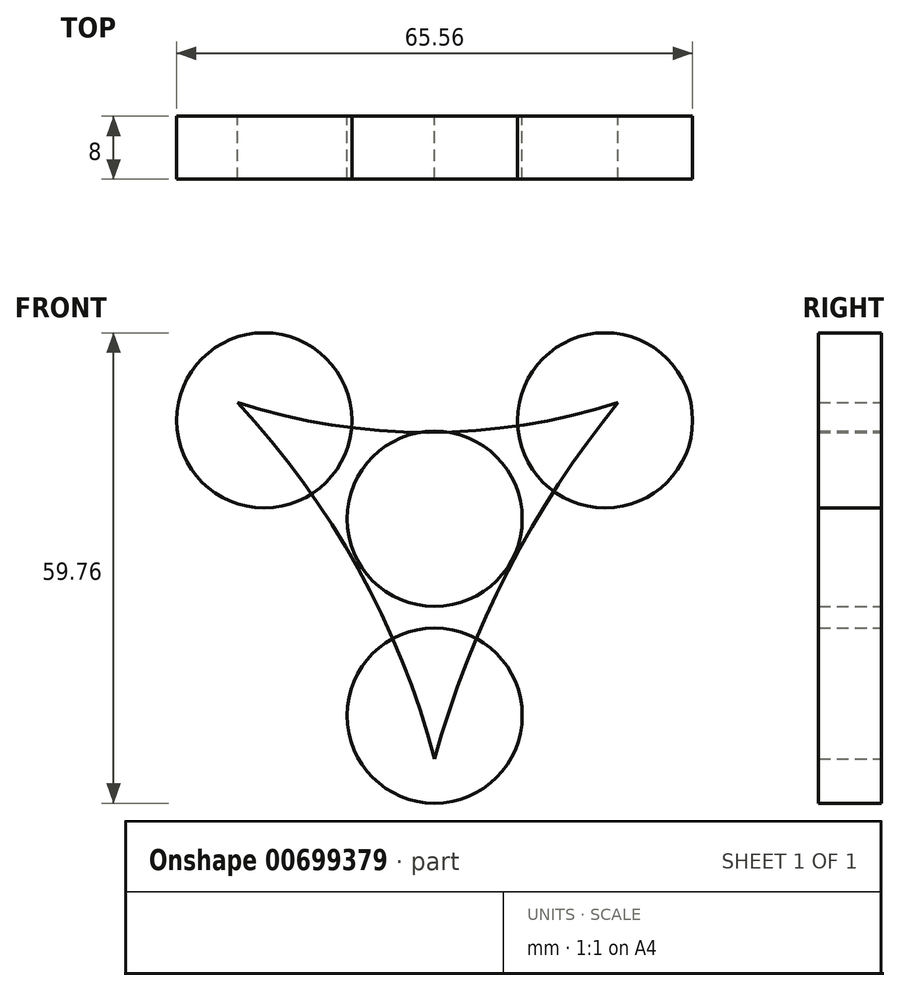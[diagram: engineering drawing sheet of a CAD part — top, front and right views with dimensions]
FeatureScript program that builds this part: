
annotation { "Feature Type Name" : "Feature", "Feature Type Description" : "" }
export const myFeature = defineFeature(function(context is Context, id is Id, definition is map)
    precondition{}
    {
        {
            var Q0;
            Q0=qCreatedBy(makeId("Front.planeOp"),FACE);
            var sketch = newSketch(context, id + "F0", { "sketchPlane" : qUnion([Q0])});
            skCircle(sketch, "E0", {"center": v(0, 0) * mm, "radius": 11.12 * mm});
            skCircle(sketch, "E1", {"center": v(21.65, 12.5) * mm, "radius": 11.12 * mm});
            skCircle(sketch, "E2", {"center": v(-21.65, 12.5) * mm, "radius": 11.12 * mm});
            skCircle(sketch, "E3", {"center": v(0, -25) * mm, "radius": 11.12 * mm});
            skLineSegment(sketch, "E4", {"start": v(0, 0) * mm, "end": v(21.65, 12.5) * mm});
            skLineSegment(sketch, "E5", {"start": v(0, 0) * mm, "end": v(0, -25) * mm});
            skLineSegment(sketch, "E6", {"start": v(0, 0) * mm, "end": v(-21.65, 12.5) * mm});
            skSolve(sketch);
        }
        {
            var Q0;
            Q0=qCreatedBy(makeId("Front.planeOp"),FACE);
            var sketch = newSketch(context, id + "F1", { "sketchPlane" : qUnion([Q0])});
            skArc(sketch, "E7", {"start": v(-1.61, -25) * mm, "mid": v(0.02, -25.06) * mm, "end": v(1.65, -25) * mm});
            skArc(sketch, "E8", {"start": v(0, -30.5) * mm, "mid": v(-9.72, -6.31) * mm, "end": v(-25.05, 14.76) * mm});
            skArc(sketch, "E9", {"start": v(23.3, 14.76) * mm, "mid": v(9.3, -6.66) * mm, "end": v(0, -30.5) * mm});
            skArc(sketch, "E10", {"start": v(-25.05, 14.76) * mm, "mid": v(-0.87, 10.97) * mm, "end": v(23.3, 14.76) * mm});
            skArc(sketch, "E11.trimOffspring", {"start": v(21.63, 12.65) * mm, "mid": v(21.22, 13.33) * mm, "end": v(20.78, 14) * mm});
            skArc(sketch, "E12.trimOffspring", {"start": v(-21.05, 13.59) * mm, "mid": v(-21.65, 12.6) * mm, "end": v(-22.2, 11.6) * mm});
            skSolve(sketch);
        }
        {
            var Q0;
            {var subQ0=sQuery(id+"F1.wireOp",EDGE,"E7");Q0=makeQuery(id+"F1.imprint","IMPRINT",FACE,{"disambiguationData":[TD([[makeQuery(id+"F1.imprint","IMPRINT",EDGE,{"derivedFrom":subQ0}),-1.0]])]});}
            var Q1;
            {var subQ4=sQuery(id+"F1.wireOp",EDGE,"E7");Q1=makeQuery(id+"F1.imprint","IMPRINT",FACE,{"disambiguationData":[TD([[makeQuery(id+"F1.imprint","IMPRINT",EDGE,{"derivedFrom":subQ4}),1.0]])]});}
            var Q2;
            Q2=makeQuery(id+"F0.imprint","IMPRINT",FACE,{"disambiguationData":[TD([[makeQuery(id+"F0.imprint","IMPRINT",EDGE,{"derivedFrom":sQuery(id+"F0.wireOp",EDGE,"E3")}),1.0]])]});
            var Q3;
            {var subQ0=sQuery(id+"F0.wireOp",EDGE,"E6");var subQ1=sQuery(id+"F0.wireOp",EDGE,"E0");var subQ2=makeQuery(id+"F0.imprint","INTERSECT",VERTEX,{"derivedFrom":[subQ1,subQ0]});Q3=makeQuery(id+"F0.imprint","IMPRINT",FACE,{"disambiguationData":[TD([[makeQuery(id+"F0.imprint","IMPRINT",EDGE,{"disambiguationData":[TD([[subQ2,1.0]])],"derivedFrom":subQ1}),1.0]])]});}
            var Q4;
            {var subQ0=sQuery(id+"F0.wireOp",EDGE,"E6");var subQ1=sQuery(id+"F0.wireOp",EDGE,"E0");var subQ2=makeQuery(id+"F0.imprint","INTERSECT",VERTEX,{"derivedFrom":[subQ1,subQ0]});Q4=makeQuery(id+"F0.imprint","IMPRINT",FACE,{"disambiguationData":[TD([[makeQuery(id+"F0.imprint","IMPRINT",EDGE,{"disambiguationData":[TD([[subQ2,-1.0]])],"derivedFrom":subQ1}),1.0]])]});}
            var Q5;
            {var subQ0=sQuery(id+"F0.wireOp",EDGE,"E4");var subQ1=sQuery(id+"F0.wireOp",EDGE,"E0");var subQ2=makeQuery(id+"F0.imprint","INTERSECT",VERTEX,{"derivedFrom":[subQ1,subQ0]});Q5=makeQuery(id+"F0.imprint","IMPRINT",FACE,{"disambiguationData":[TD([[makeQuery(id+"F0.imprint","IMPRINT",EDGE,{"disambiguationData":[TD([[subQ2,1.0]])],"derivedFrom":subQ1}),1.0]])]});}
            var Q6;
            {var subQ3=sQuery(id+"F1.wireOp",EDGE,"E12.trimOffspring");Q6=makeQuery(id+"F1.imprint","IMPRINT",FACE,{"disambiguationData":[TD([[makeQuery(id+"F1.imprint","IMPRINT",EDGE,{"derivedFrom":subQ3}),-1.0]])]});}
            var Q7;
            {var subQ3=sQuery(id+"F1.wireOp",EDGE,"E11.trimOffspring");Q7=makeQuery(id+"F1.imprint","IMPRINT",FACE,{"disambiguationData":[TD([[makeQuery(id+"F1.imprint","IMPRINT",EDGE,{"derivedFrom":subQ3}),-1.0]])]});}
            var Q8;
            Q8=makeQuery(id+"F0.imprint","IMPRINT",FACE,{"disambiguationData":[TD([[makeQuery(id+"F0.imprint","IMPRINT",EDGE,{"derivedFrom":sQuery(id+"F0.wireOp",EDGE,"E2")}),1.0]])]});
            var Q9;
            Q9=makeQuery(id+"F0.imprint","IMPRINT",FACE,{"disambiguationData":[TD([[makeQuery(id+"F0.imprint","IMPRINT",EDGE,{"derivedFrom":sQuery(id+"F0.wireOp",EDGE,"E1")}),1.0]])]});
            extrude(context, id + "F2", {"entities" : qUnion([Q0, Q1, Q2, Q3, Q4, Q5, Q6, Q7, Q8, Q9]), "depth" : 8 * mm, "offsetDistance" : 25 * mm});
        }
    });
